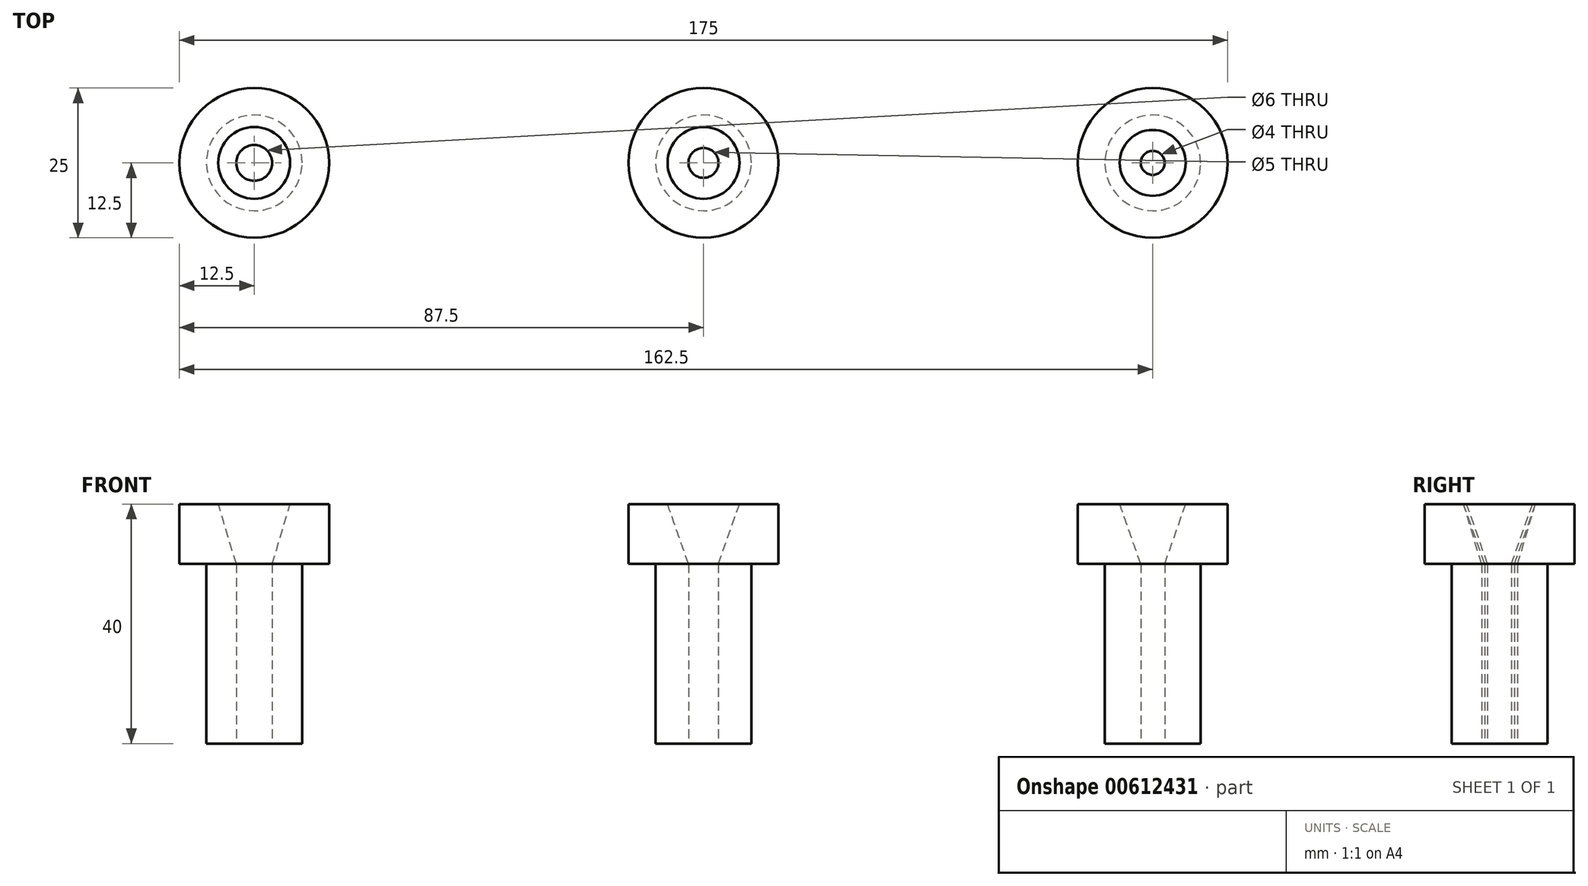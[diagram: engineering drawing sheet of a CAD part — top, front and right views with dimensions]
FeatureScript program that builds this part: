
annotation { "Feature Type Name" : "Feature", "Feature Type Description" : "" }
export const myFeature = defineFeature(function(context is Context, id is Id, definition is map)
    precondition{}
    {
        {
            var Q0;
            Q0=qCreatedBy(makeId("Front.planeOp"),FACE);
            var sketch = newSketch(context, id + "F0", { "sketchPlane" : qUnion([Q0])});
            skLineSegment(sketch, "E0.right", {"start": v(8, 0) * mm, "end": v(8, 30) * mm});
            skLineSegment(sketch, "E1.right", {"start": v(12.5, 30) * mm, "end": v(12.5, 40) * mm});
            skLineSegment(sketch, "E2", {"start": v(2.5, 30) * mm, "end": v(2.5, 0) * mm});
            skLineSegment(sketch, "E3", {"start": v(2.5, 30) * mm, "end": v(6, 40) * mm});
            skLineSegment(sketch, "E4", {"start": v(6, 40) * mm, "end": v(12.5, 40) * mm});
            skLineSegment(sketch, "E5", {"start": v(8, 30) * mm, "end": v(12.5, 30) * mm});
            skLineSegment(sketch, "E6", {"start": v(2.5, 0) * mm, "end": v(8, 0) * mm});
            skLineSegment(sketch, "E7", {"start": v(0, 0) * mm, "end": v(0, 48.9) * mm, "construction": true});
            skSolve(sketch);
        }
        {
            var Q0;
            Q0=makeQuery(id+"F0.imprint","IMPRINT",FACE,{"disambiguationData":[TD([[makeQuery(id+"F0.imprint","IMPRINT",EDGE,{"derivedFrom":sQuery(id+"F0.wireOp",EDGE,"E0.right")}),1.0]])]});
            var Q1;
            Q1=sQuery(id+"F0.wireOp",EDGE,"E7");
            revolve(context, id + "F1", {"entities" : qUnion([Q0]), "axis" : qUnion([Q1]), "revolveType" : RevolveType.FULL});
        }
        {
            var Q0;
            Q0=qCreatedBy(makeId("Front.planeOp"),FACE);
            var sketch = newSketch(context, id + "F2", { "sketchPlane" : qUnion([Q0])});
            skLineSegment(sketch, "E8.right", {"start": v(83, 0) * mm, "end": v(83, 30) * mm});
            skLineSegment(sketch, "E9.right", {"start": v(87.5, 30) * mm, "end": v(87.5, 40) * mm});
            skLineSegment(sketch, "E10", {"start": v(77, 30) * mm, "end": v(77, 0) * mm});
            skLineSegment(sketch, "E11", {"start": v(77, 30) * mm, "end": v(80.5, 40) * mm});
            skLineSegment(sketch, "E12", {"start": v(80.5, 40) * mm, "end": v(87.5, 40) * mm});
            skLineSegment(sketch, "E13", {"start": v(83, 30) * mm, "end": v(87.5, 30) * mm});
            skLineSegment(sketch, "E14", {"start": v(75, 0) * mm, "end": v(75, 48.1) * mm, "construction": true});
            skLineSegment(sketch, "E15", {"start": v(77, 0) * mm, "end": v(83, 0) * mm});
            skSolve(sketch);
        }
        {
            var Q0;
            Q0=makeQuery(id+"F2.imprint","IMPRINT",FACE,{"disambiguationData":[TD([[makeQuery(id+"F2.imprint","IMPRINT",EDGE,{"derivedFrom":sQuery(id+"F2.wireOp",EDGE,"E8.right")}),1.0]])]});
            var Q1;
            Q1=sQuery(id+"F2.wireOp",EDGE,"E14");
            revolve(context, id + "F3", {"entities" : qUnion([Q0]), "axis" : qUnion([Q1]), "revolveType" : RevolveType.FULL});
        }
        {
            var Q0;
            Q0=qCreatedBy(makeId("Front.planeOp"),FACE);
            var sketch = newSketch(context, id + "F4", { "sketchPlane" : qUnion([Q0])});
            skLineSegment(sketch, "E16.right", {"start": v(-67, 0) * mm, "end": v(-67, 30) * mm});
            skLineSegment(sketch, "E17.right", {"start": v(-62.5, 30) * mm, "end": v(-62.5, 40) * mm});
            skLineSegment(sketch, "E18", {"start": v(-72, 30) * mm, "end": v(-72, 0) * mm});
            skLineSegment(sketch, "E19", {"start": v(-72, 30) * mm, "end": v(-69, 40) * mm});
            skLineSegment(sketch, "E20", {"start": v(-69, 40) * mm, "end": v(-62.5, 40) * mm});
            skLineSegment(sketch, "E21", {"start": v(-62.5, 30) * mm, "end": v(-67, 30) * mm});
            skLineSegment(sketch, "E22", {"start": v(-72, 0) * mm, "end": v(-67, 0) * mm});
            skLineSegment(sketch, "E23", {"start": v(-75, 0) * mm, "end": v(-75, 49.03) * mm, "construction": true});
            skSolve(sketch);
        }
        {
            var Q0;
            Q0=makeQuery(id+"F4.imprint","IMPRINT",FACE,{"disambiguationData":[TD([[makeQuery(id+"F4.imprint","IMPRINT",EDGE,{"derivedFrom":sQuery(id+"F4.wireOp",EDGE,"E16.right")}),1.0]])]});
            var Q1;
            Q1=sQuery(id+"F4.wireOp",EDGE,"E23");
            revolve(context, id + "F5", {"entities" : qUnion([Q0]), "axis" : qUnion([Q1]), "revolveType" : RevolveType.FULL});
        }
    });
